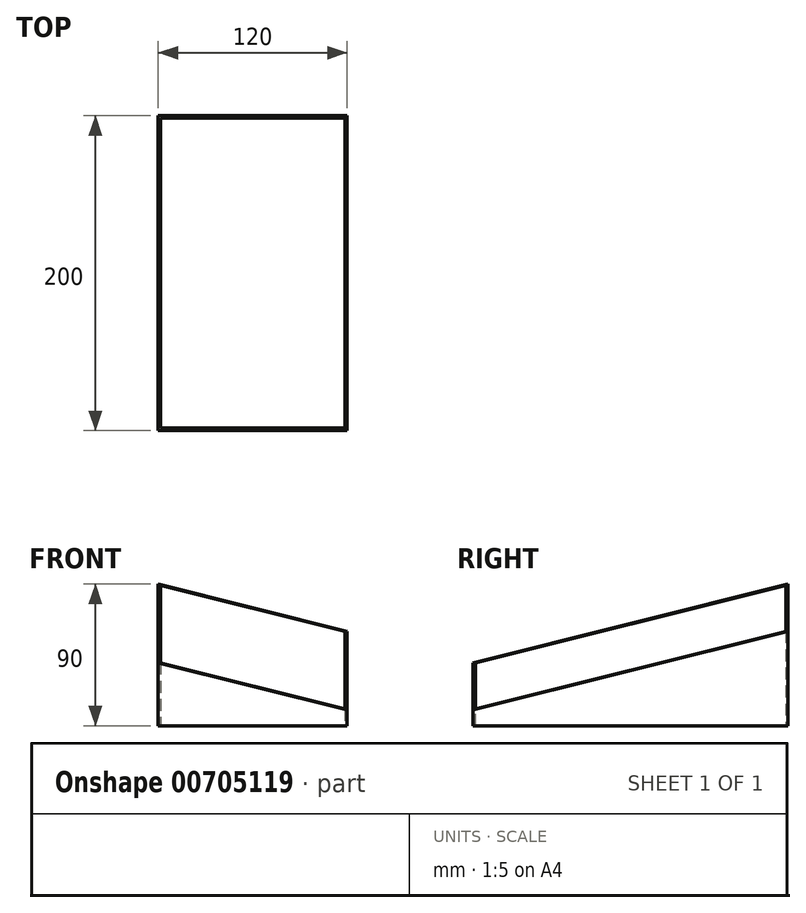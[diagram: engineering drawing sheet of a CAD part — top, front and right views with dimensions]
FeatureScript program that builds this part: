
annotation { "Feature Type Name" : "Feature", "Feature Type Description" : "" }
export const myFeature = defineFeature(function(context is Context, id is Id, definition is map)
    precondition{}
    {
        {
            var Q0;
            Q0=qCreatedBy(makeId("Top.planeOp"),FACE);
            var sketch = newSketch(context, id + "F0", { "sketchPlane" : qUnion([Q0])});
            skLineSegment(sketch, "E0.bottom", {"start": v(-60, -100) * mm, "end": v(60, -100) * mm});
            skLineSegment(sketch, "E0.top", {"start": v(-60, 100) * mm, "end": v(60, 100) * mm});
            skLineSegment(sketch, "E0.left", {"start": v(-60, -100) * mm, "end": v(-60, 100) * mm});
            skLineSegment(sketch, "E0.right", {"start": v(60, -100) * mm, "end": v(60, 100) * mm});
            skLineSegment(sketch, "E1", {"start": v(0, 100) * mm, "end": v(0, -100) * mm, "construction": true});
            skSolve(sketch);
        }
        {
            var Q0;
            Q0=sQuery(id+"F0.wireOp",VERTEX,"E0.right.start");
            var Q1;
            Q1=qCreatedBy(makeId("Front.planeOp"),FACE);
            cPlane(context, id + "F1", {"entities" : qUnion([Q0, Q1]), "cplaneType" : CPlaneType.PLANE_POINT, "offset" : 25 * mm, "width" : 150 * mm, "height" : 150 * mm});
        }
        {
            var Q0;
            Q0=sQuery(id+"F0.wireOp",VERTEX,"E0.right.start");
            var Q1;
            Q1=qCreatedBy(makeId("Right.planeOp"),FACE);
            cPlane(context, id + "F2", {"entities" : qUnion([Q0, Q1]), "cplaneType" : CPlaneType.PLANE_POINT, "offset" : 25 * mm, "width" : 150 * mm, "height" : 150 * mm});
        }
        {
            var Q0;
            Q0=sQuery(id+"F0.wireOp",VERTEX,"E0.right.end");
            var Q1;
            Q1=qCreatedBy(makeId("Front.planeOp"),FACE);
            cPlane(context, id + "F3", {"entities" : qUnion([Q0, Q1]), "cplaneType" : CPlaneType.PLANE_POINT, "offset" : 25 * mm, "width" : 150 * mm, "height" : 150 * mm});
        }
        {
            var Q0;
            Q0=sQuery(id+"F0.wireOp",VERTEX,"E0.bottom.start");
            var Q1;
            Q1=qCreatedBy(makeId("Right.planeOp"),FACE);
            cPlane(context, id + "F4", {"entities" : qUnion([Q0, Q1]), "cplaneType" : CPlaneType.PLANE_POINT, "offset" : 25 * mm, "width" : 150 * mm, "height" : 150 * mm});
        }
        {
            var Q0;
            Q0=qCreatedBy(id+"F1.planeOp",FACE);
            var sketch = newSketch(context, id + "F5", { "sketchPlane" : qUnion([Q0])});
            skPoint(sketch, "E2.0", {"position": v(60, 0) * mm});
            skLineSegment(sketch, "E3", {"start": v(60, 0) * mm, "end": v(60, 10) * mm});
            skPoint(sketch, "E4.0", {"position": v(-60, 0) * mm});
            skLineSegment(sketch, "E5", {"start": v(-60, 0) * mm, "end": v(-60, 40) * mm});
            skLineSegment(sketch, "E6", {"start": v(-60, 40) * mm, "end": v(60, 10) * mm});
            skLineSegment(sketch, "E7.0", {"start": v(-60, 0) * mm, "end": v(60, 0) * mm});
            skSolve(sketch);
        }
        {
            var Q0;
            Q0=qCreatedBy(id+"F2.planeOp",FACE);
            var sketch = newSketch(context, id + "F6", { "sketchPlane" : qUnion([Q0])});
            skPoint(sketch, "E8.0", {"position": v(-100, 10) * mm});
            skPoint(sketch, "E9.0", {"position": v(100, 0) * mm});
            skLineSegment(sketch, "E10", {"start": v(-100, 10) * mm, "end": v(100, 60) * mm});
            skLineSegment(sketch, "E11", {"start": v(100, 60) * mm, "end": v(100, 0) * mm});
            skLineSegment(sketch, "E12.0", {"start": v(-100, 0) * mm, "end": v(-100, 10) * mm});
            skLineSegment(sketch, "E13.0", {"start": v(-100, 0) * mm, "end": v(100, 0) * mm});
            skSolve(sketch);
        }
        {
            var Q0;
            Q0=qCreatedBy(id+"F3.planeOp",FACE);
            var sketch = newSketch(context, id + "F7", { "sketchPlane" : qUnion([Q0])});
            skPoint(sketch, "E14.0", {"position": v(60, 60) * mm});
            skPoint(sketch, "E15.0", {"position": v(-60, 0) * mm});
            skLineSegment(sketch, "E16", {"start": v(60, 60) * mm, "end": v(-60, 90) * mm});
            skLineSegment(sketch, "E17", {"start": v(-60, 90) * mm, "end": v(-60, 0) * mm});
            skLineSegment(sketch, "E18.0", {"start": v(60, 60) * mm, "end": v(60, 0) * mm});
            skLineSegment(sketch, "E19.0", {"start": v(-60, 0) * mm, "end": v(60, 0) * mm});
            skSolve(sketch);
        }
        {
            var Q0;
            Q0=qCreatedBy(id+"F4.planeOp",FACE);
            var sketch = newSketch(context, id + "F8", { "sketchPlane" : qUnion([Q0])});
            skPoint(sketch, "E20.0", {"position": v(100, 90) * mm});
            skPoint(sketch, "E21.0", {"position": v(-100, 40) * mm});
            skLineSegment(sketch, "E22", {"start": v(100, 90) * mm, "end": v(-100, 40) * mm});
            skLineSegment(sketch, "E23.0", {"start": v(100, 90) * mm, "end": v(100, 0) * mm});
            skLineSegment(sketch, "E24.0", {"start": v(-100, 0) * mm, "end": v(100, 0) * mm});
            skLineSegment(sketch, "E25.0", {"start": v(-100, 0) * mm, "end": v(-100, 40) * mm});
            skSolve(sketch);
        }
        {
            var Q0;
            Q0=makeQuery(id+"F8.imprint","IMPRINT",FACE,{"disambiguationData":[TD([[makeQuery(id+"F8.imprint","IMPRINT",EDGE,{"derivedFrom":sQuery(id+"F8.wireOp",EDGE,"E22")}),1.0]])]});
            var Q1;
            Q1=makeQuery(id+"F6.imprint","IMPRINT",FACE,{"disambiguationData":[TD([[makeQuery(id+"F6.imprint","IMPRINT",EDGE,{"derivedFrom":sQuery(id+"F6.wireOp",EDGE,"E10")}),-1.0]])]});
            loft(context, id + "F9", {"sheetProfilesArray" : [{ "sheetProfileEntities" : qUnion([Q0]) }, { "sheetProfileEntities" : qUnion([Q1]) }]});
        }
        {
            var Q0;
            Q0=makeQuery(id+"F9.opLoft","SWEPT_FACE",FACE,{"disambiguationData":[OSD([sQuery(id+"F6.wireOp",EDGE,"E11"),sQuery(id+"F6.wireOp",EDGE,"E12.0"),sQuery(id+"F6.wireOp",EDGE,"E13.0"),sQuery(id+"F8.wireOp",EDGE,"E23.0"),sQuery(id+"F8.wireOp",EDGE,"E24.0"),sQuery(id+"F8.wireOp",EDGE,"E25.0")])]});
            var Q1;
            Q1=makeQuery(id+"F9.opLoft","SWEPT_FACE",FACE,{"disambiguationData":[OSD([sQuery(id+"F6.wireOp",EDGE,"E10"),sQuery(id+"F6.wireOp",EDGE,"E11"),sQuery(id+"F6.wireOp",EDGE,"E12.0"),sQuery(id+"F8.wireOp",EDGE,"E22"),sQuery(id+"F8.wireOp",EDGE,"E23.0"),sQuery(id+"F8.wireOp",EDGE,"E25.0")])]});
            shell(context, id + "F10", {"entities" : qUnion([Q0, Q1]), "thickness" : 1.5 * mm});
        }
    });
